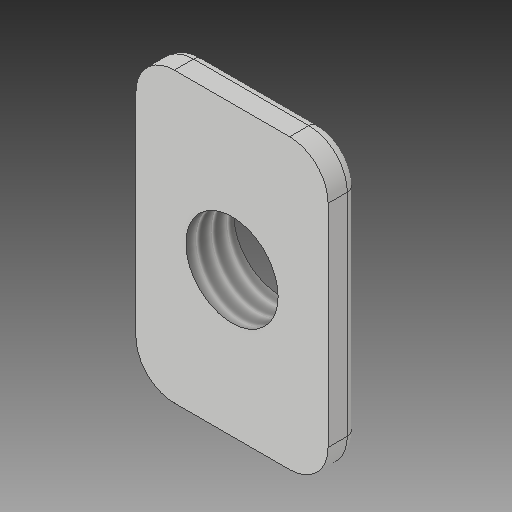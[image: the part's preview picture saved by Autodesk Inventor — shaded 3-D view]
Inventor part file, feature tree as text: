
AUTODESK INVENTOR PART (.ipt)
format: ipt  version: 2017 (Build 210142000, 142)  size: 144,384 bytes
history: native  units: mm
features: other x3, sketch x2
ambient origin geometry x8: Origin, YZ Plane, XZ Plane, XY Plane, X Axis, Y Axis, Z Axis, Center Point
bodies: Solid1 (feature_tree)
feature tree (5):
  other  "M5 Tee Nut_CPY.ipt"
  other  "Solid1::M5 Tee Nut_CPY.ipt"
  other  "TaggingFeature1"
  sketch  "Sketch1"  dims[d0=10.0mm]
  sketch  "Sketch2"
